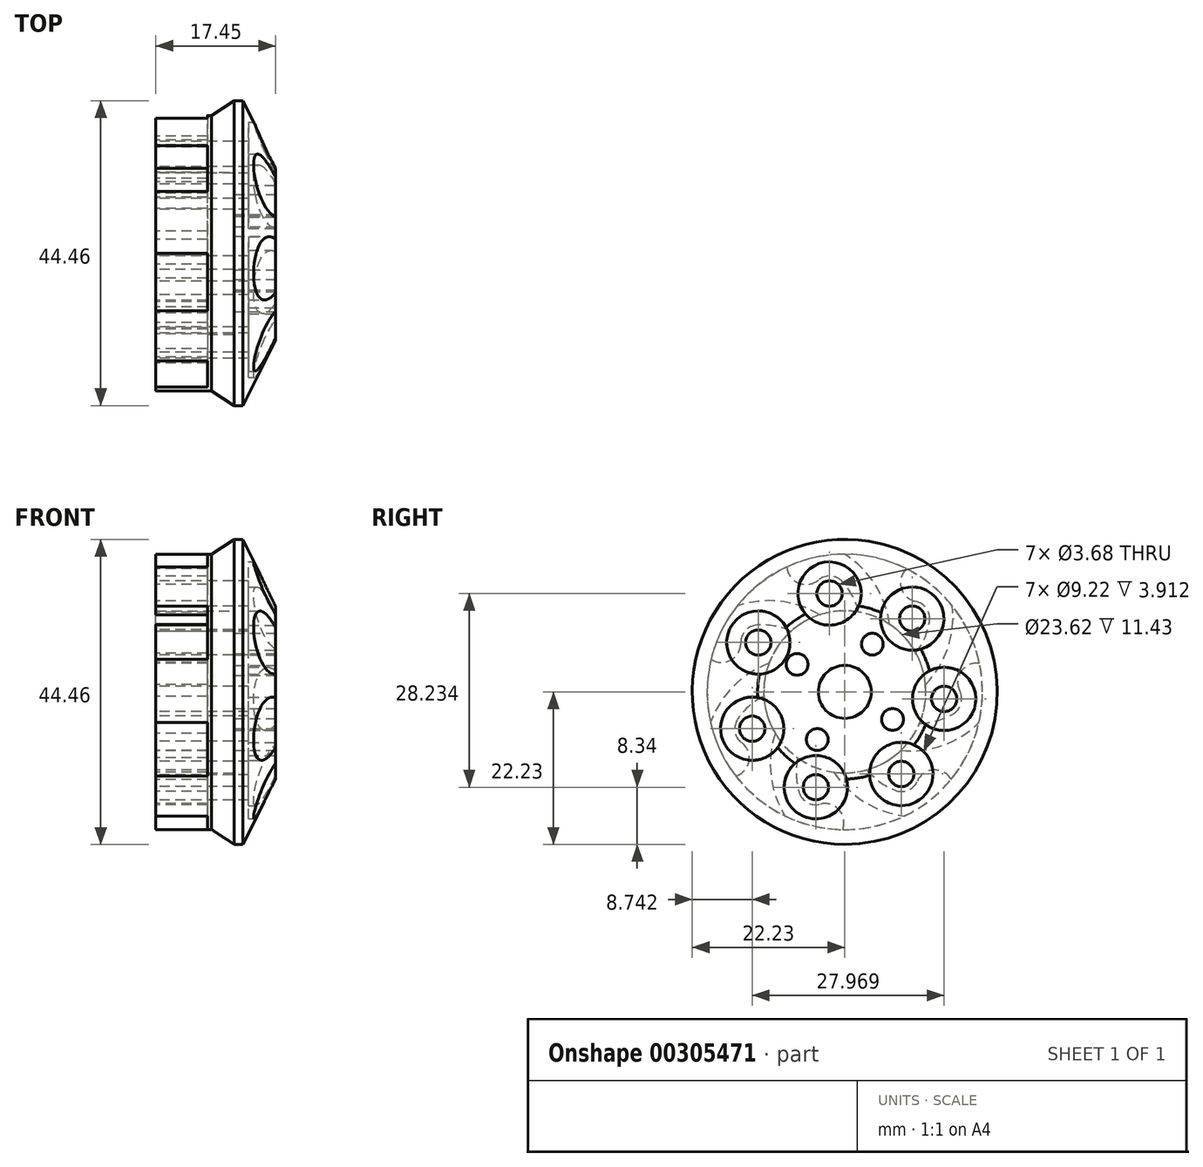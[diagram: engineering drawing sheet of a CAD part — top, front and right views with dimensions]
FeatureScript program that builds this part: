
annotation { "Feature Type Name" : "Feature", "Feature Type Description" : "" }
export const myFeature = defineFeature(function(context is Context, id is Id, definition is map)
    precondition{}
    {
        {
            var Q0;
            Q0=qCreatedBy(makeId("Top.planeOp"),FACE);
            var sketch = newSketch(context, id + "F0", { "sketchPlane" : qUnion([Q0])});
            skLineSegment(sketch, "E0", {"start": v(17.45, 0) * mm, "end": v(17.45, -12.7) * mm});
            skLineSegment(sketch, "E1", {"start": v(17.45, -12.7) * mm, "end": v(12.7, -22.23) * mm});
            skLineSegment(sketch, "E2", {"start": v(12.7, -22.23) * mm, "end": v(11.43, -22.23) * mm});
            skLineSegment(sketch, "E3", {"start": v(11.43, -22.23) * mm, "end": v(8.13, -20.07) * mm});
            skLineSegment(sketch, "E4", {"start": v(8.13, -20.07) * mm, "end": v(0, -20.07) * mm});
            skLineSegment(sketch, "E5", {"start": v(0, -20.07) * mm, "end": v(0, -11.81) * mm});
            skLineSegment(sketch, "E6", {"start": v(0, -11.81) * mm, "end": v(11.43, -11.81) * mm});
            skLineSegment(sketch, "E7", {"start": v(11.43, -11.81) * mm, "end": v(11.43, 0) * mm});
            skLineSegment(sketch, "E8", {"start": v(11.43, 0) * mm, "end": v(17.45, 0) * mm});
            skLineSegment(sketch, "E9", {"start": v(40.63, 0) * mm, "end": v(0, 0) * mm, "construction": true});
            skSolve(sketch);
        }
        {
            var Q0;
            Q0=qSketchRegion(id+"F0",true);
            var Q1;
            Q1=sQuery(id+"F0.wireOp",EDGE,"E9");
            revolve(context, id + "F1", {"entities" : qUnion([Q0]), "axis" : qUnion([Q1]), "revolveType" : RevolveType.FULL});
        }
        {
            var Q0;
            Q0=qCreatedBy(makeId("Right.planeOp"),FACE);
            var sketch = newSketch(context, id + "F2", { "sketchPlane" : qUnion([Q0])});
            skCircle(sketch, "E10.cCircle", {"center": v(0, 0) * mm, "radius": 20.07 * mm, "construction": true});
            skLineSegment(sketch, "E10.0", {"start": v(-9.66, 20.07) * mm, "end": v(9.66, 20.07) * mm, "construction": true});
            skLineSegment(sketch, "E10.1", {"start": v(9.66, 20.07) * mm, "end": v(21.71, 4.96) * mm, "construction": true});
            skLineSegment(sketch, "E10.2", {"start": v(21.71, 4.96) * mm, "end": v(17.41, -13.89) * mm, "construction": true});
            skLineSegment(sketch, "E10.3", {"start": v(17.41, -13.89) * mm, "end": v(0, -22.27) * mm, "construction": true});
            skLineSegment(sketch, "E10.4", {"start": v(0, -22.27) * mm, "end": v(-17.41, -13.89) * mm, "construction": true});
            skLineSegment(sketch, "E10.5", {"start": v(-17.41, -13.89) * mm, "end": v(-21.71, 4.96) * mm, "construction": true});
            skLineSegment(sketch, "E10.6", {"start": v(-21.71, 4.96) * mm, "end": v(-9.66, 20.07) * mm, "construction": true});
            skPoint(sketch, "E10.0.midPoint", {"position": v(0, 20.07) * mm});
            skLineSegment(sketch, "E11", {"start": v(0, 0) * mm, "end": v(0, 20.07) * mm, "construction": true});
            skLineSegment(sketch, "E12", {"start": v(0, 0) * mm, "end": v(-8.43, 18.2) * mm, "construction": true});
            skLineSegment(sketch, "E13", {"start": v(0, 0) * mm, "end": v(2.02, 11.64) * mm, "construction": true});
            skCircle(sketch, "E14", {"center": v(0, 0) * mm, "radius": 11.81 * mm, "construction": true});
            skPoint(sketch, "E15", {"position": v(0, 11.81) * mm});
            skLineSegment(sketch, "E16", {"start": v(0, 0) * mm, "end": v(6.5, 9.86) * mm, "construction": true});
            skArc(sketch, "E17", {"start": v(6.5, 9.86) * mm, "mid": v(4.4, 15.68) * mm, "end": v(0, 20.07) * mm});
            skCircle(sketch, "E18", {"center": v(0, 0) * mm, "radius": 14.52 * mm, "construction": true});
            skLineSegment(sketch, "E19", {"start": v(0, 0) * mm, "end": v(-2.23, 14.34) * mm, "construction": true});
            skPoint(sketch, "E20", {"position": v(0, 14.52) * mm});
            skCircle(sketch, "E21", {"center": v(-2.23, 14.34) * mm, "radius": 1.84 * mm, "construction": true});
            skArc(sketch, "E22", {"start": v(-0.35, 16.07) * mm, "mid": v(-2.06, 16.9) * mm, "end": v(-3.86, 16.3) * mm});
            skArc(sketch, "E23", {"start": v(2.02, 11.64) * mm, "mid": v(1.12, 14) * mm, "end": v(-0.35, 16.07) * mm});
            skArc(sketch, "E24", {"start": v(-8.43, 18.2) * mm, "mid": v(-6.72, 15.87) * mm, "end": v(-3.86, 16.3) * mm});
            skArc(sketch, "E25", {"start": v(0, 20.07) * mm, "mid": v(-4.73, 21.48) * mm, "end": v(-8.43, 18.2) * mm});
            skArc(sketch, "E26", {"start": v(2.02, 11.64) * mm, "mid": v(4.04, 10.18) * mm, "end": v(6.5, 9.86) * mm});
            skCircle(sketch, "E27", {"center": v(-2.23, 14.34) * mm, "radius": 1.84 * mm});
            skArc(sketch, "E28.1.0", {"start": v(-3.65, 11.23) * mm, "mid": v(-9.53, 13.21) * mm, "end": v(-15.69, 12.51) * mm});
            skArc(sketch, "E28.1.1", {"start": v(-7.84, 8.84) * mm, "mid": v(-5.44, 9.5) * mm, "end": v(-3.65, 11.23) * mm});
            skArc(sketch, "E28.1.2", {"start": v(-7.84, 8.84) * mm, "mid": v(-10.25, 9.6) * mm, "end": v(-12.78, 9.75) * mm});
            skArc(sketch, "E28.1.3", {"start": v(-12.78, 9.75) * mm, "mid": v(-14.49, 8.92) * mm, "end": v(-15.16, 7.15) * mm});
            skArc(sketch, "E28.1.4", {"start": v(-15.69, 12.51) * mm, "mid": v(-19.75, 9.7) * mm, "end": v(-19.5, 4.76) * mm});
            skArc(sketch, "E28.1.5", {"start": v(-19.5, 4.76) * mm, "mid": v(-16.6, 4.64) * mm, "end": v(-15.16, 7.15) * mm});
            skCircle(sketch, "E28.1.6", {"center": v(-12.6, 7.2) * mm, "radius": 1.84 * mm, "construction": true});
            skCircle(sketch, "E28.1.7", {"center": v(-12.6, 7.2) * mm, "radius": 1.84 * mm});
            skArc(sketch, "E28.2.0", {"start": v(-11.06, 4.15) * mm, "mid": v(-16.27, 0.8) * mm, "end": v(-19.56, -4.47) * mm});
            skArc(sketch, "E28.2.1", {"start": v(-11.8, -0.62) * mm, "mid": v(-10.82, 1.68) * mm, "end": v(-11.06, 4.15) * mm});
            skArc(sketch, "E28.2.2", {"start": v(-11.8, -0.62) * mm, "mid": v(-13.9, -2.03) * mm, "end": v(-15.59, -3.91) * mm});
            skArc(sketch, "E28.2.3", {"start": v(-15.59, -3.91) * mm, "mid": v(-16, -5.76) * mm, "end": v(-15.04, -7.4) * mm});
            skArc(sketch, "E28.2.4", {"start": v(-19.56, -4.47) * mm, "mid": v(-19.9, -9.4) * mm, "end": v(-15.87, -12.27) * mm});
            skArc(sketch, "E28.2.5", {"start": v(-15.87, -12.27) * mm, "mid": v(-13.98, -10.09) * mm, "end": v(-15.04, -7.4) * mm});
            skCircle(sketch, "E28.2.6", {"center": v(-13.49, -5.36) * mm, "radius": 1.84 * mm, "construction": true});
            skCircle(sketch, "E28.2.7", {"center": v(-13.49, -5.36) * mm, "radius": 1.84 * mm});
            skArc(sketch, "E28.3.0", {"start": v(-10.14, -6.05) * mm, "mid": v(-10.76, -12.23) * mm, "end": v(-8.7, -18.08) * mm});
            skArc(sketch, "E28.3.1", {"start": v(-6.87, -9.6) * mm, "mid": v(-8.06, -7.42) * mm, "end": v(-10.14, -6.05) * mm});
            skArc(sketch, "E28.3.2", {"start": v(-6.87, -9.6) * mm, "mid": v(-7.08, -12.13) * mm, "end": v(-6.66, -14.63) * mm});
            skArc(sketch, "E28.3.3", {"start": v(-6.66, -14.63) * mm, "mid": v(-5.48, -16.11) * mm, "end": v(-3.6, -16.37) * mm});
            skArc(sketch, "E28.3.4", {"start": v(-8.7, -18.08) * mm, "mid": v(-5.06, -21.41) * mm, "end": v(-0.3, -20.06) * mm});
            skArc(sketch, "E28.3.5", {"start": v(-0.3, -20.06) * mm, "mid": v(-0.83, -17.22) * mm, "end": v(-3.6, -16.37) * mm});
            skCircle(sketch, "E28.3.6", {"center": v(-4.22, -13.9) * mm, "radius": 1.84 * mm, "construction": true});
            skCircle(sketch, "E28.3.7", {"center": v(-4.22, -13.9) * mm, "radius": 1.84 * mm});
            skArc(sketch, "E28.4.0", {"start": v(-1.59, -11.7) * mm, "mid": v(2.85, -16.04) * mm, "end": v(8.7, -18.08) * mm});
            skArc(sketch, "E28.4.1", {"start": v(3.22, -11.36) * mm, "mid": v(0.77, -10.92) * mm, "end": v(-1.59, -11.7) * mm});
            skArc(sketch, "E28.4.2", {"start": v(3.22, -11.36) * mm, "mid": v(5.07, -13.1) * mm, "end": v(7.28, -14.33) * mm});
            skArc(sketch, "E28.4.3", {"start": v(7.28, -14.33) * mm, "mid": v(9.18, -14.33) * mm, "end": v(10.55, -13.01) * mm});
            skArc(sketch, "E28.4.4", {"start": v(8.7, -18.08) * mm, "mid": v(13.59, -17.3) * mm, "end": v(15.5, -12.75) * mm});
            skArc(sketch, "E28.4.5", {"start": v(15.5, -12.75) * mm, "mid": v(12.94, -11.38) * mm, "end": v(10.55, -13.01) * mm});
            skCircle(sketch, "E28.4.6", {"center": v(8.23, -11.96) * mm, "radius": 1.84 * mm, "construction": true});
            skCircle(sketch, "E28.4.7", {"center": v(8.23, -11.96) * mm, "radius": 1.84 * mm});
            skArc(sketch, "E28.5.0", {"start": v(8.16, -8.54) * mm, "mid": v(14.31, -7.77) * mm, "end": v(19.56, -4.47) * mm});
            skArc(sketch, "E28.5.1", {"start": v(10.9, -4.56) * mm, "mid": v(9.02, -6.2) * mm, "end": v(8.16, -8.54) * mm});
            skArc(sketch, "E28.5.2", {"start": v(10.9, -4.56) * mm, "mid": v(13.4, -4.2) * mm, "end": v(15.74, -3.24) * mm});
            skArc(sketch, "E28.5.3", {"start": v(15.74, -3.24) * mm, "mid": v(16.92, -1.75) * mm, "end": v(16.76, 0.14) * mm});
            skArc(sketch, "E28.5.4", {"start": v(19.56, -4.47) * mm, "mid": v(22, -0.17) * mm, "end": v(19.63, 4.17) * mm});
            skArc(sketch, "E28.5.5", {"start": v(19.63, 4.17) * mm, "mid": v(16.97, 3.02) * mm, "end": v(16.76, 0.14) * mm});
            skCircle(sketch, "E28.5.6", {"center": v(14.48, -1.02) * mm, "radius": 1.84 * mm, "construction": true});
            skCircle(sketch, "E28.5.7", {"center": v(14.48, -1.02) * mm, "radius": 1.84 * mm});
            skArc(sketch, "E28.6.0", {"start": v(11.76, 1.06) * mm, "mid": v(15, 6.35) * mm, "end": v(15.69, 12.51) * mm});
            skArc(sketch, "E28.6.1", {"start": v(10.36, 5.67) * mm, "mid": v(10.48, 3.19) * mm, "end": v(11.76, 1.06) * mm});
            skArc(sketch, "E28.6.2", {"start": v(10.36, 5.67) * mm, "mid": v(11.64, 7.86) * mm, "end": v(12.35, 10.29) * mm});
            skArc(sketch, "E28.6.3", {"start": v(12.35, 10.29) * mm, "mid": v(11.92, 12.14) * mm, "end": v(10.34, 13.19) * mm});
            skArc(sketch, "E28.6.4", {"start": v(15.69, 12.51) * mm, "mid": v(13.85, 17.1) * mm, "end": v(8.98, 17.95) * mm});
            skArc(sketch, "E28.6.5", {"start": v(8.98, 17.95) * mm, "mid": v(8.22, 15.15) * mm, "end": v(10.34, 13.19) * mm});
            skCircle(sketch, "E28.6.6", {"center": v(9.83, 10.69) * mm, "radius": 1.84 * mm, "construction": true});
            skCircle(sketch, "E28.6.7", {"center": v(9.83, 10.69) * mm, "radius": 1.84 * mm});
            skSolve(sketch);
        }
        {
            var Q0;
            Q0=qSketchRegion(id+"F2",true);
            extrude(context, id + "F3", {"entities" : qUnion([Q0]), "operationType" : NewBodyOperationType.REMOVE, "depth" : 7.52 * mm});
        }
        {
            var Q0;
            Q0=qCreatedBy(makeId("Right.planeOp"),FACE);
            var sketch = newSketch(context, id + "F4", { "sketchPlane" : qUnion([Q0])});
            skCircle(sketch, "E29", {"center": v(9.83, 10.69) * mm, "radius": 1.84 * mm});
            skCircle(sketch, "E30.1.0", {"center": v(-2.23, 14.34) * mm, "radius": 1.84 * mm});
            skCircle(sketch, "E30.2.0", {"center": v(-12.6, 7.2) * mm, "radius": 1.84 * mm});
            skCircle(sketch, "E30.3.0", {"center": v(-13.49, -5.36) * mm, "radius": 1.84 * mm});
            skCircle(sketch, "E30.4.0", {"center": v(-4.22, -13.9) * mm, "radius": 1.84 * mm});
            skCircle(sketch, "E30.5.0", {"center": v(8.23, -11.96) * mm, "radius": 1.84 * mm});
            skCircle(sketch, "E30.6.0", {"center": v(14.48, -1.02) * mm, "radius": 1.84 * mm});
            skPoint(sketch, "E30.center", {"position": v(0, 0) * mm});
            skSolve(sketch);
        }
        {
            var Q0;
            Q0=makeQuery(id+"F4.imprint","IMPRINT",FACE,{"disambiguationData":[TD([[makeQuery(id+"F4.imprint","IMPRINT",EDGE,{"derivedFrom":sQuery(id+"F4.wireOp",EDGE,"E29")}),1.0]])]});
            var Q1;
            Q1=makeQuery(id+"F4.imprint","IMPRINT",FACE,{"disambiguationData":[TD([[makeQuery(id+"F4.imprint","IMPRINT",EDGE,{"derivedFrom":sQuery(id+"F4.wireOp",EDGE,"E30.1.0")}),1.0]])]});
            var Q2;
            Q2=makeQuery(id+"F4.imprint","IMPRINT",FACE,{"disambiguationData":[TD([[makeQuery(id+"F4.imprint","IMPRINT",EDGE,{"derivedFrom":sQuery(id+"F4.wireOp",EDGE,"E30.2.0")}),1.0]])]});
            var Q3;
            Q3=makeQuery(id+"F4.imprint","IMPRINT",FACE,{"disambiguationData":[TD([[makeQuery(id+"F4.imprint","IMPRINT",EDGE,{"derivedFrom":sQuery(id+"F4.wireOp",EDGE,"E30.3.0")}),1.0]])]});
            var Q4;
            Q4=makeQuery(id+"F4.imprint","IMPRINT",FACE,{"disambiguationData":[TD([[makeQuery(id+"F4.imprint","IMPRINT",EDGE,{"derivedFrom":sQuery(id+"F4.wireOp",EDGE,"E30.4.0")}),1.0]])]});
            var Q5;
            Q5=makeQuery(id+"F4.imprint","IMPRINT",FACE,{"disambiguationData":[TD([[makeQuery(id+"F4.imprint","IMPRINT",EDGE,{"derivedFrom":sQuery(id+"F4.wireOp",EDGE,"E30.5.0")}),1.0]])]});
            var Q6;
            Q6=makeQuery(id+"F4.imprint","IMPRINT",FACE,{"disambiguationData":[TD([[makeQuery(id+"F4.imprint","IMPRINT",EDGE,{"derivedFrom":sQuery(id+"F4.wireOp",EDGE,"E30.6.0")}),1.0]])]});
            extrude(context, id + "F5", {"entities" : qUnion([Q0, Q1, Q2, Q3, Q4, Q5, Q6]), "operationType" : NewBodyOperationType.REMOVE, "endBound" : BoundingType.THROUGH_ALL, "depth" : 25.4 * mm});
        }
        {
            var Q0;
            Q0=qCreatedBy(makeId("Right.planeOp"),FACE);
            cPlane(context, id + "F6", {"entities" : qUnion([Q0]), "cplaneType" : CPlaneType.OFFSET, "offset" : 17.45 * mm, "width" : 152.4 * mm, "height" : 152.4 * mm});
        }
        {
            var Q0;
            Q0=qCreatedBy(id+"F6.planeOp",FACE);
            var sketch = newSketch(context, id + "F7", { "sketchPlane" : qUnion([Q0])});
            skCircle(sketch, "E31", {"center": v(14.48, -1.02) * mm, "radius": 4.61 * mm});
            skCircle(sketch, "E32.1.0", {"center": v(9.83, 10.69) * mm, "radius": 4.61 * mm});
            skCircle(sketch, "E32.2.0", {"center": v(-2.23, 14.34) * mm, "radius": 4.61 * mm});
            skCircle(sketch, "E32.3.0", {"center": v(-12.6, 7.2) * mm, "radius": 4.61 * mm});
            skCircle(sketch, "E32.4.0", {"center": v(-13.49, -5.36) * mm, "radius": 4.61 * mm});
            skCircle(sketch, "E32.5.0", {"center": v(-4.22, -13.9) * mm, "radius": 4.61 * mm});
            skCircle(sketch, "E32.6.0", {"center": v(8.23, -11.96) * mm, "radius": 4.61 * mm});
            skPoint(sketch, "E32.center", {"position": v(0, 0) * mm});
            skSolve(sketch);
        }
        {
            var Q0;
            Q0=qSketchRegion(id+"F7",true);
            extrude(context, id + "F8", {"entities" : qUnion([Q0]), "operationType" : NewBodyOperationType.REMOVE, "oppositeDirection" : true, "depth" : 3.91 * mm});
        }
        {
            var Q0;
            Q0=qCreatedBy(id+"F6.planeOp",FACE);
            var sketch = newSketch(context, id + "F9", { "sketchPlane" : qUnion([Q0])});
            skCircle(sketch, "E33", {"center": v(0, 0) * mm, "radius": 3.86 * mm});
            skCircle(sketch, "E34", {"center": v(6.95, -4.01) * mm, "radius": 1.59 * mm});
            skLineSegment(sketch, "E35", {"start": v(0, 0) * mm, "end": v(22.23, 0) * mm, "construction": true});
            skLineSegment(sketch, "E36", {"start": v(0, 0) * mm, "end": v(6.95, -4.01) * mm, "construction": true});
            skCircle(sketch, "E37.1.0", {"center": v(4.01, 6.95) * mm, "radius": 1.59 * mm});
            skCircle(sketch, "E37.2.0", {"center": v(-6.95, 4.01) * mm, "radius": 1.59 * mm});
            skCircle(sketch, "E37.3.0", {"center": v(-4.01, -6.95) * mm, "radius": 1.59 * mm});
            skSolve(sketch);
        }
        {
            var Q0;
            Q0=qSketchRegion(id+"F9",true);
            extrude(context, id + "F10", {"entities" : qUnion([Q0]), "operationType" : NewBodyOperationType.REMOVE, "endBound" : BoundingType.THROUGH_ALL, "oppositeDirection" : true, "depth" : 25.4 * mm});
        }
    });
